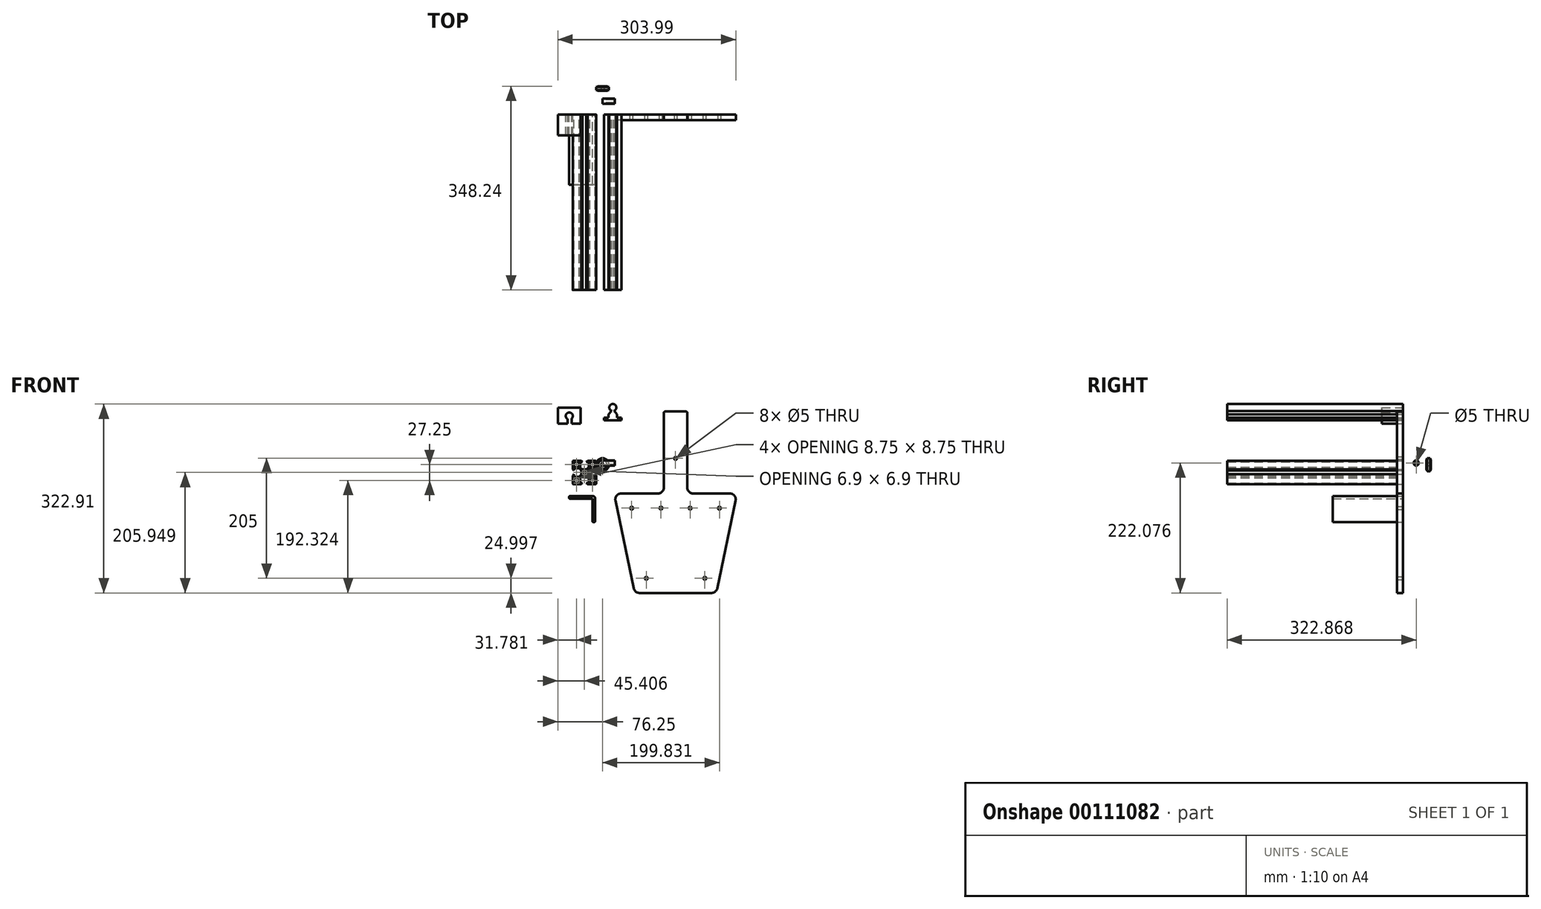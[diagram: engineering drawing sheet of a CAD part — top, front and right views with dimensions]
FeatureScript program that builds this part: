
annotation { "Feature Type Name" : "Feature", "Feature Type Description" : "" }
export const myFeature = defineFeature(function(context is Context, id is Id, definition is map)
    precondition{}
    {
        {
            var Q0;
            Q0=qCreatedBy(makeId("Front.planeOp"),FACE);
            var sketch = newSketch(context, id + "F0", { "sketchPlane" : qUnion([Q0])});
            skLineSegment(sketch, "E0", {"start": v(-49.84, 48.39) * mm, "end": v(-36.1, 48.39) * mm});
            skLineSegment(sketch, "E1", {"start": v(-36.1, 48.39) * mm, "end": v(-34.1, 46.39) * mm});
            skLineSegment(sketch, "E2", {"start": v(-34.1, 46.39) * mm, "end": v(-38.1, 46.39) * mm});
            skLineSegment(sketch, "E3", {"start": v(-48.84, 45.39) * mm, "end": v(-48.84, 38.64) * mm});
            skLineSegment(sketch, "E4", {"start": v(-48.84, 31.64) * mm, "end": v(-50.84, 33.64) * mm});
            skLineSegment(sketch, "E5", {"start": v(-50.84, 33.64) * mm, "end": v(-50.84, 47.39) * mm});
            skLineSegment(sketch, "E6", {"start": v(-50.84, 23.14) * mm, "end": v(-48.84, 25.14) * mm});
            skLineSegment(sketch, "E7", {"start": v(-48.84, 25.14) * mm, "end": v(-48.84, 22.14) * mm});
            skLineSegment(sketch, "E8", {"start": v(-47.84, 10.39) * mm, "end": v(-41.1, 10.39) * mm});
            skLineSegment(sketch, "E9", {"start": v(-34.1, 10.39) * mm, "end": v(-35.8, 8.68) * mm});
            skLineSegment(sketch, "E10", {"start": v(-36.5, 8.39) * mm, "end": v(-49.84, 8.39) * mm});
            skLineSegment(sketch, "E11", {"start": v(-50.84, 9.39) * mm, "end": v(-50.84, 23.14) * mm});
            skLineSegment(sketch, "E12", {"start": v(-25.6, 48.39) * mm, "end": v(-11.84, 48.39) * mm});
            skLineSegment(sketch, "E13", {"start": v(-10.84, 47.39) * mm, "end": v(-10.84, 33.64) * mm});
            skLineSegment(sketch, "E14", {"start": v(-10.84, 33.64) * mm, "end": v(-12.84, 31.64) * mm});
            skLineSegment(sketch, "E15", {"start": v(-12.84, 31.64) * mm, "end": v(-12.84, 34.64) * mm});
            skLineSegment(sketch, "E16", {"start": v(-13.84, 46.39) * mm, "end": v(-20.6, 46.39) * mm});
            skLineSegment(sketch, "E17", {"start": v(-27.6, 46.39) * mm, "end": v(-25.6, 48.39) * mm});
            skLineSegment(sketch, "E18", {"start": v(-10.84, 9.39) * mm, "end": v(-10.84, 22.72) * mm});
            skLineSegment(sketch, "E19", {"start": v(-11.14, 23.43) * mm, "end": v(-12.84, 25.14) * mm});
            skLineSegment(sketch, "E20", {"start": v(-12.84, 25.14) * mm, "end": v(-12.84, 22.14) * mm});
            skLineSegment(sketch, "E21", {"start": v(-13.84, 10.39) * mm, "end": v(-20.6, 10.39) * mm});
            skLineSegment(sketch, "E22", {"start": v(-27.6, 10.39) * mm, "end": v(-25.89, 8.68) * mm});
            skLineSegment(sketch, "E23", {"start": v(-25.18, 8.39) * mm, "end": v(-11.84, 8.39) * mm});
            skLineSegment(sketch, "E24", {"start": v(-48.84, 10.39) * mm, "end": v(-12.84, 46.39) * mm, "construction": true});
            skLineSegment(sketch, "E25", {"start": v(-48.84, 46.39) * mm, "end": v(-12.84, 10.39) * mm, "construction": true});
            skLineSegment(sketch, "E26", {"start": v(-40.1, 45.39) * mm, "end": v(-40.1, 38.64) * mm});
            skLineSegment(sketch, "E27", {"start": v(-41.1, 37.64) * mm, "end": v(-47.84, 37.64) * mm});
            skLineSegment(sketch, "E28", {"start": v(-13.84, 37.64) * mm, "end": v(-20.6, 37.64) * mm});
            skLineSegment(sketch, "E29", {"start": v(-21.6, 38.64) * mm, "end": v(-21.6, 45.39) * mm});
            skLineSegment(sketch, "E30", {"start": v(-47.84, 35.64) * mm, "end": v(-39.92, 35.64) * mm});
            skLineSegment(sketch, "E31", {"start": v(-38.1, 37.1) * mm, "end": v(-38.1, 46.39) * mm});
            skLineSegment(sketch, "E32", {"start": v(-23.6, 45.39) * mm, "end": v(-23.6, 37.47) * mm});
            skLineSegment(sketch, "E33", {"start": v(-21.77, 35.64) * mm, "end": v(-13.84, 35.64) * mm});
            skLineSegment(sketch, "E34.bottom", {"start": v(-34.74, 33.84) * mm, "end": v(-27.22, 33.84) * mm});
            skLineSegment(sketch, "E34.top", {"start": v(-34.46, 22.94) * mm, "end": v(-27.22, 22.94) * mm});
            skLineSegment(sketch, "E34.left", {"start": v(-36.3, 32) * mm, "end": v(-36.3, 24.77) * mm});
            skLineSegment(sketch, "E34.right", {"start": v(-25.4, 32) * mm, "end": v(-25.4, 24.77) * mm});
            skLineSegment(sketch, "E35.bottom", {"start": v(-33.3, 31.84) * mm, "end": v(-28.4, 31.84) * mm});
            skLineSegment(sketch, "E35.top", {"start": v(-33.3, 24.94) * mm, "end": v(-28.4, 24.94) * mm});
            skLineSegment(sketch, "E35.left", {"start": v(-34.3, 30.84) * mm, "end": v(-34.3, 25.94) * mm});
            skLineSegment(sketch, "E35.right", {"start": v(-27.4, 30.84) * mm, "end": v(-27.4, 25.94) * mm});
            skLineSegment(sketch, "E36", {"start": v(-23.89, 36.76) * mm, "end": v(-26.52, 34.13) * mm});
            skLineSegment(sketch, "E37", {"start": v(-25.1, 32.72) * mm, "end": v(-22.47, 35.35) * mm});
            skLineSegment(sketch, "E38", {"start": v(-35.44, 34.12) * mm, "end": v(-37.79, 36.39) * mm});
            skLineSegment(sketch, "E39", {"start": v(-47.84, 19.14) * mm, "end": v(-41.1, 19.14) * mm});
            skLineSegment(sketch, "E40", {"start": v(-40.1, 18.14) * mm, "end": v(-40.1, 11.39) * mm});
            skLineSegment(sketch, "E41", {"start": v(-47.84, 21.14) * mm, "end": v(-39.92, 21.14) * mm});
            skLineSegment(sketch, "E42", {"start": v(-38.1, 19.31) * mm, "end": v(-38.1, 11.39) * mm});
            skLineSegment(sketch, "E43", {"start": v(-21.6, 11.39) * mm, "end": v(-21.6, 18.14) * mm});
            skLineSegment(sketch, "E44", {"start": v(-20.6, 19.14) * mm, "end": v(-13.84, 19.14) * mm});
            skLineSegment(sketch, "E45", {"start": v(-21.77, 21.14) * mm, "end": v(-13.84, 21.14) * mm});
            skLineSegment(sketch, "E46", {"start": v(-23.6, 19.31) * mm, "end": v(-23.6, 11.39) * mm});
            skLineSegment(sketch, "E47", {"start": v(-35.17, 22.65) * mm, "end": v(-37.8, 20.02) * mm});
            skLineSegment(sketch, "E48", {"start": v(-39.22, 21.43) * mm, "end": v(-36.59, 24.06) * mm});
            skLineSegment(sketch, "E49", {"start": v(-22.47, 21.43) * mm, "end": v(-25.1, 24.06) * mm});
            skLineSegment(sketch, "E50", {"start": v(-36.59, 32.72) * mm, "end": v(-39.22, 35.35) * mm});
            skLineSegment(sketch, "E51", {"start": v(-23.89, 20.02) * mm, "end": v(-26.52, 22.65) * mm});
            skLineSegment(sketch, "E52.trimOffspring", {"start": v(-41.1, 46.39) * mm, "end": v(-47.84, 46.39) * mm});
            skLineSegment(sketch, "E53.trimOffspring", {"start": v(-48.84, 34.64) * mm, "end": v(-48.84, 31.64) * mm});
            skLineSegment(sketch, "E54.trimOffspring", {"start": v(-24.6, 46.39) * mm, "end": v(-27.6, 46.39) * mm});
            skLineSegment(sketch, "E55.trimOffspring", {"start": v(-12.84, 38.64) * mm, "end": v(-12.84, 45.39) * mm});
            skPoint(sketch, "E56.orphan", {"position": v(-23.6, 35.64) * mm});
            skLineSegment(sketch, "E57.trimOffspring", {"start": v(-12.84, 18.14) * mm, "end": v(-12.84, 11.39) * mm});
            skLineSegment(sketch, "E58.trimOffspring", {"start": v(-24.6, 10.39) * mm, "end": v(-27.6, 10.39) * mm});
            skLineSegment(sketch, "E59.trimOffspring", {"start": v(-37.1, 10.39) * mm, "end": v(-34.1, 10.39) * mm});
            skPoint(sketch, "E60.orphan", {"position": v(-38.1, 21.14) * mm});
            skLineSegment(sketch, "E61.trimOffspring", {"start": v(-48.84, 18.14) * mm, "end": v(-48.84, 11.39) * mm});
            skPoint(sketch, "E62.visualSharp", {"position": v(-48.84, 21.14) * mm});
            skArc(sketch, "E62.filletArc", {"start": v(-48.84, 22.14) * mm, "mid": v(-48.55, 21.43) * mm, "end": v(-47.84, 21.14) * mm});
            skPoint(sketch, "E63.visualSharp", {"position": v(-48.84, 19.14) * mm});
            skArc(sketch, "E63.filletArc", {"start": v(-47.84, 19.14) * mm, "mid": v(-48.55, 18.85) * mm, "end": v(-48.84, 18.14) * mm});
            skPoint(sketch, "E64.visualSharp", {"position": v(-40.1, 19.14) * mm});
            skArc(sketch, "E64.filletArc", {"start": v(-40.1, 18.14) * mm, "mid": v(-40.39, 18.85) * mm, "end": v(-41.1, 19.14) * mm});
            skPoint(sketch, "E65.visualSharp", {"position": v(-40.1, 10.39) * mm});
            skArc(sketch, "E65.filletArc", {"start": v(-41.1, 10.39) * mm, "mid": v(-40.39, 10.68) * mm, "end": v(-40.1, 11.39) * mm});
            skPoint(sketch, "E66.visualSharp", {"position": v(-48.84, 10.39) * mm});
            skArc(sketch, "E66.filletArc", {"start": v(-48.84, 11.39) * mm, "mid": v(-48.55, 10.68) * mm, "end": v(-47.84, 10.39) * mm});
            skPoint(sketch, "E67.visualSharp", {"position": v(-50.84, 8.39) * mm});
            skArc(sketch, "E67.filletArc", {"start": v(-50.84, 9.39) * mm, "mid": v(-50.55, 8.68) * mm, "end": v(-49.84, 8.39) * mm});
            skPoint(sketch, "E68.visualSharp", {"position": v(-36.1, 8.39) * mm});
            skArc(sketch, "E68.filletArc", {"start": v(-36.5, 8.39) * mm, "mid": v(-36.13, 8.46) * mm, "end": v(-35.8, 8.68) * mm});
            skPoint(sketch, "E69.visualSharp", {"position": v(-38.1, 10.39) * mm});
            skArc(sketch, "E69.filletArc", {"start": v(-38.1, 11.39) * mm, "mid": v(-37.8, 10.68) * mm, "end": v(-37.1, 10.39) * mm});
            skPoint(sketch, "E70.visualSharp", {"position": v(-38.1, 19.72) * mm});
            skArc(sketch, "E70.filletArc", {"start": v(-37.8, 20.02) * mm, "mid": v(-38.02, 19.7) * mm, "end": v(-38.1, 19.31) * mm});
            skPoint(sketch, "E71.visualSharp", {"position": v(-39.5, 21.14) * mm});
            skArc(sketch, "E71.filletArc", {"start": v(-39.92, 21.14) * mm, "mid": v(-39.54, 21.21) * mm, "end": v(-39.22, 21.43) * mm});
            skPoint(sketch, "E72.visualSharp", {"position": v(-34.88, 22.94) * mm});
            skArc(sketch, "E72.filletArc", {"start": v(-34.46, 22.94) * mm, "mid": v(-34.85, 22.86) * mm, "end": v(-35.17, 22.65) * mm});
            skPoint(sketch, "E73.visualSharp", {"position": v(-36.3, 24.35) * mm});
            skArc(sketch, "E73.filletArc", {"start": v(-36.59, 24.06) * mm, "mid": v(-36.37, 24.39) * mm, "end": v(-36.3, 24.77) * mm});
            skPoint(sketch, "E74.visualSharp", {"position": v(-10.84, 8.39) * mm});
            skArc(sketch, "E74.filletArc", {"start": v(-11.84, 8.39) * mm, "mid": v(-11.14, 8.68) * mm, "end": v(-10.84, 9.39) * mm});
            skPoint(sketch, "E75.visualSharp", {"position": v(-12.84, 10.39) * mm});
            skArc(sketch, "E75.filletArc", {"start": v(-13.84, 10.39) * mm, "mid": v(-13.14, 10.68) * mm, "end": v(-12.84, 11.39) * mm});
            skPoint(sketch, "E76.visualSharp", {"position": v(-21.6, 10.39) * mm});
            skArc(sketch, "E76.filletArc", {"start": v(-21.6, 11.39) * mm, "mid": v(-21.3, 10.68) * mm, "end": v(-20.6, 10.39) * mm});
            skPoint(sketch, "E77.visualSharp", {"position": v(-23.6, 10.39) * mm});
            skArc(sketch, "E77.filletArc", {"start": v(-24.6, 10.39) * mm, "mid": v(-23.89, 10.68) * mm, "end": v(-23.6, 11.39) * mm});
            skPoint(sketch, "E78.visualSharp", {"position": v(-25.6, 8.39) * mm});
            skArc(sketch, "E78.filletArc", {"start": v(-25.89, 8.68) * mm, "mid": v(-25.56, 8.46) * mm, "end": v(-25.18, 8.39) * mm});
            skPoint(sketch, "E79.visualSharp", {"position": v(-12.84, 19.14) * mm});
            skArc(sketch, "E79.filletArc", {"start": v(-12.84, 18.14) * mm, "mid": v(-13.14, 18.85) * mm, "end": v(-13.84, 19.14) * mm});
            skPoint(sketch, "E80.visualSharp", {"position": v(-21.6, 19.14) * mm});
            skArc(sketch, "E80.filletArc", {"start": v(-20.6, 19.14) * mm, "mid": v(-21.3, 18.85) * mm, "end": v(-21.6, 18.14) * mm});
            skPoint(sketch, "E81.orphan", {"position": v(-23.6, 21.14) * mm});
            skPoint(sketch, "E82.visualSharp", {"position": v(-12.84, 21.14) * mm});
            skArc(sketch, "E82.filletArc", {"start": v(-13.84, 21.14) * mm, "mid": v(-13.14, 21.43) * mm, "end": v(-12.84, 22.14) * mm});
            skPoint(sketch, "E83.visualSharp", {"position": v(-10.84, 23.14) * mm});
            skArc(sketch, "E83.filletArc", {"start": v(-10.84, 22.72) * mm, "mid": v(-10.92, 23.1) * mm, "end": v(-11.14, 23.43) * mm});
            skPoint(sketch, "E84.visualSharp", {"position": v(-23.6, 19.72) * mm});
            skArc(sketch, "E84.filletArc", {"start": v(-23.6, 19.31) * mm, "mid": v(-23.67, 19.7) * mm, "end": v(-23.89, 20.02) * mm});
            skPoint(sketch, "E85.visualSharp", {"position": v(-26.81, 22.94) * mm});
            skArc(sketch, "E85.filletArc", {"start": v(-26.52, 22.65) * mm, "mid": v(-26.84, 22.86) * mm, "end": v(-27.22, 22.94) * mm});
            skPoint(sketch, "E86.visualSharp", {"position": v(-22.18, 21.14) * mm});
            skArc(sketch, "E86.filletArc", {"start": v(-22.47, 21.43) * mm, "mid": v(-22.15, 21.21) * mm, "end": v(-21.77, 21.14) * mm});
            skPoint(sketch, "E87.visualSharp", {"position": v(-25.4, 24.35) * mm});
            skArc(sketch, "E87.filletArc", {"start": v(-25.4, 24.77) * mm, "mid": v(-25.32, 24.39) * mm, "end": v(-25.1, 24.06) * mm});
            skPoint(sketch, "E88.visualSharp", {"position": v(-27.4, 24.94) * mm});
            skArc(sketch, "E88.filletArc", {"start": v(-28.4, 24.94) * mm, "mid": v(-27.69, 25.23) * mm, "end": v(-27.4, 25.94) * mm});
            skPoint(sketch, "E89.visualSharp", {"position": v(-34.3, 24.94) * mm});
            skArc(sketch, "E89.filletArc", {"start": v(-34.3, 25.94) * mm, "mid": v(-34, 25.23) * mm, "end": v(-33.3, 24.94) * mm});
            skPoint(sketch, "E90.visualSharp", {"position": v(-34.3, 31.84) * mm});
            skArc(sketch, "E90.filletArc", {"start": v(-33.3, 31.84) * mm, "mid": v(-34, 31.54) * mm, "end": v(-34.3, 30.84) * mm});
            skPoint(sketch, "E91.visualSharp", {"position": v(-27.4, 31.84) * mm});
            skArc(sketch, "E91.filletArc", {"start": v(-27.4, 30.84) * mm, "mid": v(-27.69, 31.54) * mm, "end": v(-28.4, 31.84) * mm});
            skPoint(sketch, "E92.visualSharp", {"position": v(-25.4, 32.42) * mm});
            skArc(sketch, "E92.filletArc", {"start": v(-25.1, 32.72) * mm, "mid": v(-25.32, 32.4) * mm, "end": v(-25.4, 32) * mm});
            skPoint(sketch, "E93.visualSharp", {"position": v(-22.18, 35.64) * mm});
            skArc(sketch, "E93.filletArc", {"start": v(-21.77, 35.64) * mm, "mid": v(-22.15, 35.56) * mm, "end": v(-22.47, 35.35) * mm});
            skPoint(sketch, "E94.visualSharp", {"position": v(-12.84, 35.64) * mm});
            skArc(sketch, "E94.filletArc", {"start": v(-12.84, 34.64) * mm, "mid": v(-13.14, 35.35) * mm, "end": v(-13.84, 35.64) * mm});
            skPoint(sketch, "E95.visualSharp", {"position": v(-12.84, 37.64) * mm});
            skArc(sketch, "E95.filletArc", {"start": v(-13.84, 37.64) * mm, "mid": v(-13.14, 37.93) * mm, "end": v(-12.84, 38.64) * mm});
            skPoint(sketch, "E96.visualSharp", {"position": v(-21.6, 37.64) * mm});
            skArc(sketch, "E96.filletArc", {"start": v(-21.6, 38.64) * mm, "mid": v(-21.3, 37.93) * mm, "end": v(-20.6, 37.64) * mm});
            skPoint(sketch, "E97.visualSharp", {"position": v(-23.6, 37.05) * mm});
            skArc(sketch, "E97.filletArc", {"start": v(-23.89, 36.76) * mm, "mid": v(-23.67, 37.08) * mm, "end": v(-23.6, 37.47) * mm});
            skPoint(sketch, "E98.visualSharp", {"position": v(-26.81, 33.84) * mm});
            skArc(sketch, "E98.filletArc", {"start": v(-27.22, 33.84) * mm, "mid": v(-26.84, 33.91) * mm, "end": v(-26.52, 34.13) * mm});
            skPoint(sketch, "E99.visualSharp", {"position": v(-35.15, 33.84) * mm});
            skArc(sketch, "E99.filletArc", {"start": v(-35.44, 34.12) * mm, "mid": v(-35.12, 33.91) * mm, "end": v(-34.74, 33.84) * mm});
            skPoint(sketch, "E100.visualSharp", {"position": v(-38.1, 36.68) * mm});
            skArc(sketch, "E100.filletArc", {"start": v(-38.1, 37.1) * mm, "mid": v(-38.01, 36.72) * mm, "end": v(-37.79, 36.39) * mm});
            skPoint(sketch, "E101.visualSharp", {"position": v(-36.3, 32.42) * mm});
            skArc(sketch, "E101.filletArc", {"start": v(-36.3, 32) * mm, "mid": v(-36.37, 32.4) * mm, "end": v(-36.59, 32.72) * mm});
            skPoint(sketch, "E102.visualSharp", {"position": v(-39.5, 35.64) * mm});
            skArc(sketch, "E102.filletArc", {"start": v(-39.22, 35.35) * mm, "mid": v(-39.54, 35.56) * mm, "end": v(-39.92, 35.64) * mm});
            skPoint(sketch, "E103.visualSharp", {"position": v(-12.84, 46.39) * mm});
            skArc(sketch, "E103.filletArc", {"start": v(-12.84, 45.39) * mm, "mid": v(-13.14, 46.1) * mm, "end": v(-13.84, 46.39) * mm});
            skPoint(sketch, "E104.visualSharp", {"position": v(-10.84, 48.39) * mm});
            skArc(sketch, "E104.filletArc", {"start": v(-10.84, 47.39) * mm, "mid": v(-11.14, 48.1) * mm, "end": v(-11.84, 48.39) * mm});
            skPoint(sketch, "E105.visualSharp", {"position": v(-23.6, 46.39) * mm});
            skArc(sketch, "E105.filletArc", {"start": v(-23.6, 45.39) * mm, "mid": v(-23.89, 46.1) * mm, "end": v(-24.6, 46.39) * mm});
            skPoint(sketch, "E106.visualSharp", {"position": v(-21.6, 46.39) * mm});
            skArc(sketch, "E106.filletArc", {"start": v(-20.6, 46.39) * mm, "mid": v(-21.3, 46.1) * mm, "end": v(-21.6, 45.39) * mm});
            skPoint(sketch, "E107.visualSharp", {"position": v(-48.84, 35.64) * mm});
            skArc(sketch, "E107.filletArc", {"start": v(-47.84, 35.64) * mm, "mid": v(-48.55, 35.35) * mm, "end": v(-48.84, 34.64) * mm});
            skPoint(sketch, "E108.visualSharp", {"position": v(-48.84, 37.64) * mm});
            skArc(sketch, "E108.filletArc", {"start": v(-48.84, 38.64) * mm, "mid": v(-48.55, 37.93) * mm, "end": v(-47.84, 37.64) * mm});
            skPoint(sketch, "E109.visualSharp", {"position": v(-50.84, 48.39) * mm});
            skArc(sketch, "E109.filletArc", {"start": v(-49.84, 48.39) * mm, "mid": v(-50.55, 48.1) * mm, "end": v(-50.84, 47.39) * mm});
            skPoint(sketch, "E110.visualSharp", {"position": v(-48.84, 46.39) * mm});
            skArc(sketch, "E110.filletArc", {"start": v(-47.84, 46.39) * mm, "mid": v(-48.55, 46.1) * mm, "end": v(-48.84, 45.39) * mm});
            skPoint(sketch, "E111.visualSharp", {"position": v(-40.1, 46.39) * mm});
            skArc(sketch, "E111.filletArc", {"start": v(-40.1, 45.39) * mm, "mid": v(-40.39, 46.1) * mm, "end": v(-41.1, 46.39) * mm});
            skPoint(sketch, "E112.visualSharp", {"position": v(-40.1, 37.64) * mm});
            skArc(sketch, "E112.filletArc", {"start": v(-41.1, 37.64) * mm, "mid": v(-40.39, 37.93) * mm, "end": v(-40.1, 38.64) * mm});
            skSolve(sketch);
        }
        {
            var Q0;
            Q0=makeQuery(id+"F0.imprint","IMPRINT",FACE,{"disambiguationData":[TD([[makeQuery(id+"F0.imprint","IMPRINT",EDGE,{"derivedFrom":sQuery(id+"F0.wireOp",EDGE,"E0")}),-1.0]])]});
            extrude(context, id + "F1", {"entities" : qUnion([Q0]), "depth" : 300 * mm});
        }
        {
            var Q0;
            Q0=qCreatedBy(makeId("Front.planeOp"),FACE);
            var sketch = newSketch(context, id + "F2", { "sketchPlane" : qUnion([Q0])});
            skLineSegment(sketch, "E113", {"start": v(-55.84, -12.26) * mm, "end": v(-15.84, -12.26) * mm});
            skLineSegment(sketch, "E114", {"start": v(-12.84, -15.26) * mm, "end": v(-12.84, -55.26) * mm});
            skLineSegment(sketch, "E115", {"start": v(-13.84, -56.26) * mm, "end": v(-15.84, -56.26) * mm});
            skLineSegment(sketch, "E116", {"start": v(-16.84, -55.26) * mm, "end": v(-16.84, -17.26) * mm});
            skLineSegment(sketch, "E117", {"start": v(-17.84, -16.26) * mm, "end": v(-55.84, -16.26) * mm});
            skLineSegment(sketch, "E118", {"start": v(-56.84, -15.26) * mm, "end": v(-56.84, -13.26) * mm});
            skPoint(sketch, "E119.visualSharp", {"position": v(-56.84, -12.26) * mm});
            skArc(sketch, "E119.filletArc", {"start": v(-55.84, -12.26) * mm, "mid": v(-56.55, -12.56) * mm, "end": v(-56.84, -13.26) * mm});
            skPoint(sketch, "E120.visualSharp", {"position": v(-56.84, -16.26) * mm});
            skArc(sketch, "E120.filletArc", {"start": v(-56.84, -15.26) * mm, "mid": v(-56.55, -15.97) * mm, "end": v(-55.84, -16.26) * mm});
            skPoint(sketch, "E121.visualSharp", {"position": v(-16.84, -16.26) * mm});
            skArc(sketch, "E121.filletArc", {"start": v(-16.84, -17.26) * mm, "mid": v(-17.13, -16.56) * mm, "end": v(-17.84, -16.26) * mm});
            skPoint(sketch, "E122.visualSharp", {"position": v(-12.84, -56.26) * mm});
            skArc(sketch, "E122.filletArc", {"start": v(-13.84, -56.26) * mm, "mid": v(-13.13, -55.97) * mm, "end": v(-12.84, -55.26) * mm});
            skPoint(sketch, "E123.visualSharp", {"position": v(-16.84, -56.26) * mm});
            skArc(sketch, "E123.filletArc", {"start": v(-16.84, -55.26) * mm, "mid": v(-16.55, -55.97) * mm, "end": v(-15.84, -56.26) * mm});
            skPoint(sketch, "E124.visualSharp", {"position": v(-12.84, -12.26) * mm});
            skArc(sketch, "E124.filletArc", {"start": v(-12.84, -15.26) * mm, "mid": v(-13.72, -13.14) * mm, "end": v(-15.84, -12.26) * mm});
            skSolve(sketch);
        }
        {
            var Q0;
            Q0=makeQuery(id+"F2.imprint","IMPRINT",FACE,{"disambiguationData":[TD([[makeQuery(id+"F2.imprint","IMPRINT",EDGE,{"derivedFrom":sQuery(id+"F2.wireOp",EDGE,"E113")}),-1.0]])]});
            extrude(context, id + "F3", {"entities" : qUnion([Q0]), "depth" : 120 * mm});
        }
        {
            var Q0;
            Q0=qCreatedBy(makeId("Front.planeOp"),FACE);
            var sketch = newSketch(context, id + "F4", { "sketchPlane" : qUnion([Q0])});
            skLineSegment(sketch, "E125", {"start": v(-8.08, -7.56) * mm, "end": v(54.83, -7.56) * mm});
            skLineSegment(sketch, "E126", {"start": v(187.53, -19.6) * mm, "end": v(156.28, -169.6) * mm});
            skLineSegment(sketch, "E127", {"start": v(146.5, -177.56) * mm, "end": v(23.17, -177.56) * mm});
            skLineSegment(sketch, "E128", {"start": v(13.38, -169.6) * mm, "end": v(-17.87, -19.6) * mm});
            skPoint(sketch, "E129", {"position": v(84.83, -7.56) * mm});
            skPoint(sketch, "E130", {"position": v(84.83, -177.56) * mm});
            skLineSegment(sketch, "E131", {"start": v(84.83, -177.56) * mm, "end": v(84.83, -7.56) * mm, "construction": true});
            skPoint(sketch, "E132.visualSharp", {"position": v(190.04, -7.56) * mm});
            skArc(sketch, "E132.filletArc", {"start": v(187.53, -19.6) * mm, "mid": v(185.5, -11.25) * mm, "end": v(177.74, -7.56) * mm});
            skPoint(sketch, "E133.visualSharp", {"position": v(-20.38, -7.56) * mm});
            skArc(sketch, "E133.filletArc", {"start": v(-8.08, -7.56) * mm, "mid": v(-15.84, -11.25) * mm, "end": v(-17.87, -19.6) * mm});
            skPoint(sketch, "E134.visualSharp", {"position": v(15.04, -177.56) * mm});
            skArc(sketch, "E134.filletArc", {"start": v(13.38, -169.6) * mm, "mid": v(16.86, -175.32) * mm, "end": v(23.17, -177.56) * mm});
            skPoint(sketch, "E135.visualSharp", {"position": v(154.62, -177.56) * mm});
            skArc(sketch, "E135.filletArc", {"start": v(146.5, -177.56) * mm, "mid": v(152.8, -175.32) * mm, "end": v(156.28, -169.6) * mm});
            skLineSegment(sketch, "E136", {"start": v(9.83, -152.56) * mm, "end": v(159.83, -152.56) * mm, "construction": true});
            skLineSegment(sketch, "E137", {"start": v(-15.17, -32.56) * mm, "end": v(184.83, -32.56) * mm, "construction": true});
            skCircle(sketch, "E138", {"center": v(9.83, -32.56) * mm, "radius": 2.5 * mm});
            skCircle(sketch, "E139", {"center": v(59.83, -32.56) * mm, "radius": 2.5 * mm});
            skCircle(sketch, "E140", {"center": v(109.83, -32.56) * mm, "radius": 2.5 * mm});
            skCircle(sketch, "E141", {"center": v(159.83, -32.56) * mm, "radius": 2.5 * mm});
            skCircle(sketch, "E142", {"center": v(34.83, -152.56) * mm, "radius": 2.5 * mm});
            skCircle(sketch, "E143", {"center": v(134.83, -152.56) * mm, "radius": 2.5 * mm});
            skLineSegment(sketch, "E144", {"start": v(34.83, -141.56) * mm, "end": v(134.83, -141.56) * mm, "construction": true});
            skLineSegment(sketch, "E145", {"start": v(9.83, -59.91) * mm, "end": v(59.83, -59.91) * mm, "construction": true});
            skLineSegment(sketch, "E146", {"start": v(59.83, -59.91) * mm, "end": v(109.83, -59.91) * mm, "construction": true});
            skLineSegment(sketch, "E147", {"start": v(109.83, -59.91) * mm, "end": v(159.83, -59.91) * mm, "construction": true});
            skPoint(sketch, "E148", {"position": v(84.83, -59.91) * mm});
            skPoint(sketch, "E149", {"position": v(84.83, -141.56) * mm});
            skPoint(sketch, "E150", {"position": v(34.83, -59.91) * mm});
            skPoint(sketch, "E151", {"position": v(134.83, -59.91) * mm});
            skLineSegment(sketch, "E152", {"start": v(64.83, 2.44) * mm, "end": v(64.83, 130.44) * mm});
            skLineSegment(sketch, "E153", {"start": v(66.83, 132.44) * mm, "end": v(102.83, 132.44) * mm});
            skLineSegment(sketch, "E154", {"start": v(104.83, 130.44) * mm, "end": v(104.83, 2.44) * mm});
            skLineSegment(sketch, "E155.trimOffspring", {"start": v(114.83, -7.56) * mm, "end": v(177.74, -7.56) * mm});
            skPoint(sketch, "E156", {"position": v(84.83, 132.44) * mm});
            skPoint(sketch, "E157.visualSharp", {"position": v(104.83, -7.56) * mm});
            skArc(sketch, "E157.filletArc", {"start": v(104.83, 2.44) * mm, "mid": v(107.76, -4.63) * mm, "end": v(114.83, -7.56) * mm});
            skPoint(sketch, "E158.visualSharp", {"position": v(64.83, -7.56) * mm});
            skArc(sketch, "E158.filletArc", {"start": v(54.83, -7.56) * mm, "mid": v(61.9, -4.63) * mm, "end": v(64.83, 2.44) * mm});
            skPoint(sketch, "E159.visualSharp", {"position": v(104.83, 132.44) * mm});
            skArc(sketch, "E159.filletArc", {"start": v(104.83, 130.44) * mm, "mid": v(104.25, 131.85) * mm, "end": v(102.83, 132.44) * mm});
            skPoint(sketch, "E160.visualSharp", {"position": v(64.83, 132.44) * mm});
            skArc(sketch, "E160.filletArc", {"start": v(66.83, 132.44) * mm, "mid": v(65.42, 131.85) * mm, "end": v(64.83, 130.44) * mm});
            skSolve(sketch);
        }
        {
            var Q0;
            Q0=makeQuery(id+"F4.imprint","IMPRINT",FACE,{"disambiguationData":[TD([[makeQuery(id+"F4.imprint","IMPRINT",EDGE,{"derivedFrom":sQuery(id+"F4.wireOp",EDGE,"E125")}),-1.0]])]});
            extrude(context, id + "F5", {"entities" : qUnion([Q0]), "depth" : 10 * mm});
        }
        {
            var Q0;
            Q0=makeQuery(id+"F5.opExtrude","SWEPT_BODY",BODY,{"disambiguationData":[OSD([sQuery(id+"F4.wireOp",EDGE,"E125"),sQuery(id+"F4.wireOp",EDGE,"E126"),sQuery(id+"F4.wireOp",EDGE,"E127"),sQuery(id+"F4.wireOp",EDGE,"E128"),sQuery(id+"F4.wireOp",EDGE,"E132.filletArc"),sQuery(id+"F4.wireOp",EDGE,"E133.filletArc"),sQuery(id+"F4.wireOp",EDGE,"E134.filletArc"),sQuery(id+"F4.wireOp",EDGE,"E135.filletArc"),sQuery(id+"F4.wireOp",EDGE,"E138"),sQuery(id+"F4.wireOp",EDGE,"E139"),sQuery(id+"F4.wireOp",EDGE,"E140"),sQuery(id+"F4.wireOp",EDGE,"E141"),sQuery(id+"F4.wireOp",EDGE,"E142"),sQuery(id+"F4.wireOp",EDGE,"E143"),sQuery(id+"F4.wireOp",EDGE,"E152"),sQuery(id+"F4.wireOp",EDGE,"E153"),sQuery(id+"F4.wireOp",EDGE,"E154"),sQuery(id+"F4.wireOp",EDGE,"E155.trimOffspring"),sQuery(id+"F4.wireOp",EDGE,"E157.filletArc"),sQuery(id+"F4.wireOp",EDGE,"E158.filletArc"),sQuery(id+"F4.wireOp",EDGE,"E159.filletArc"),sQuery(id+"F4.wireOp",EDGE,"E160.filletArc")])]});
            transform(context, id + "F6", {"entities" : qUnion([Q0]), "transformType" : TransformType.TRANSLATION_3D, "dx" : 40 * mm, "dy" : 0 * mm, "dz" : 0 * mm, "makeCopy" : false});
        }
        {
            var Q0;
            Q0=qCreatedBy(makeId("Right.planeOp"),FACE);
            var sketch = newSketch(context, id + "F7", { "sketchPlane" : qUnion([Q0])});
            skLineSegment(sketch, "E161", {"start": v(41.74, 52.7) * mm, "end": v(46.74, 52.7) * mm});
            skLineSegment(sketch, "E162", {"start": v(46.74, 52.7) * mm, "end": v(48.24, 49.13) * mm});
            skLineSegment(sketch, "E163", {"start": v(48.24, 49.13) * mm, "end": v(48.24, 44.2) * mm});
            skLineSegment(sketch, "E164", {"start": v(41.74, 52.7) * mm, "end": v(40.24, 49.13) * mm});
            skLineSegment(sketch, "E165", {"start": v(40.24, 49.13) * mm, "end": v(40.24, 44.2) * mm});
            skLineSegment(sketch, "E166", {"start": v(40.24, 44.2) * mm, "end": v(48.24, 44.2) * mm});
            skPoint(sketch, "E167", {"position": v(44.24, 44.2) * mm});
            skPoint(sketch, "E168", {"position": v(44.24, 52.7) * mm});
            skLineSegment(sketch, "E169", {"start": v(40.24, 41.7) * mm, "end": v(48.24, 41.7) * mm, "construction": true});
            skSolve(sketch);
        }
        {
            var Q0;
            Q0=makeQuery(id+"F7.imprint","IMPRINT",FACE,{"disambiguationData":[TD([[makeQuery(id+"F7.imprint","IMPRINT",EDGE,{"derivedFrom":sQuery(id+"F7.wireOp",EDGE,"E161")}),-1.0]])]});
            var Q1;
            Q1=sQuery(id+"F7.wireOp",EDGE,"E169");
            revolve(context, id + "F8", {"entities" : qUnion([Q0]), "axis" : qUnion([Q1]), "revolveType" : RevolveType.FULL});
        }
        {
            var Q0;
            Q0=qCreatedBy(makeId("Right.planeOp"),FACE);
            var sketch = newSketch(context, id + "F9", { "sketchPlane" : qUnion([Q0])});
            skLineSegment(sketch, "E170.0", {"start": v(40.24, 34.26) * mm, "end": v(40.24, 49.13) * mm, "construction": true});
            skPoint(sketch, "E171", {"position": v(40.24, 60.88) * mm});
            skLineSegment(sketch, "E172", {"start": v(40.24, 60.88) * mm, "end": v(19.24, 60.88) * mm, "construction": true});
            skLineSegment(sketch, "E173", {"start": v(44.24, 65.5) * mm, "end": v(19.24, 65.5) * mm, "construction": true});
            skPoint(sketch, "E174", {"position": v(46.74, 52.7) * mm});
            skLineSegment(sketch, "E175", {"start": v(41.74, 52.7) * mm, "end": v(46.74, 52.7) * mm, "construction": true});
            skPoint(sketch, "E176", {"position": v(44.24, 52.7) * mm});
            skCircle(sketch, "E177", {"center": v(22.87, 44.52) * mm, "radius": 2.5 * mm});
            skCircle(sketch, "E178", {"center": v(22.87, 44.52) * mm, "radius": 4.5 * mm});
            skSolve(sketch);
        }
        {
            var Q0;
            Q0=makeQuery(id+"F9.imprint","IMPRINT",FACE,{"disambiguationData":[TD([[makeQuery(id+"F9.imprint","IMPRINT",EDGE,{"derivedFrom":sQuery(id+"F9.wireOp",EDGE,"E177")}),-1.0]])]});
            extrude(context, id + "F10", {"entities" : qUnion([Q0]), "depth" : 21 * mm});
        }
        {
            var Q0;
            Q0=makeQuery(id+"F5.opExtrude","CAP_FACE",FACE,{"disambiguationData":[OSD([sQuery(id+"F4.wireOp",EDGE,"E125"),sQuery(id+"F4.wireOp",EDGE,"E126"),sQuery(id+"F4.wireOp",EDGE,"E127"),sQuery(id+"F4.wireOp",EDGE,"E128"),sQuery(id+"F4.wireOp",EDGE,"E132.filletArc"),sQuery(id+"F4.wireOp",EDGE,"E133.filletArc"),sQuery(id+"F4.wireOp",EDGE,"E134.filletArc"),sQuery(id+"F4.wireOp",EDGE,"E135.filletArc"),sQuery(id+"F4.wireOp",EDGE,"E138"),sQuery(id+"F4.wireOp",EDGE,"E139"),sQuery(id+"F4.wireOp",EDGE,"E140"),sQuery(id+"F4.wireOp",EDGE,"E141"),sQuery(id+"F4.wireOp",EDGE,"E142"),sQuery(id+"F4.wireOp",EDGE,"E143"),sQuery(id+"F4.wireOp",EDGE,"E152"),sQuery(id+"F4.wireOp",EDGE,"E153"),sQuery(id+"F4.wireOp",EDGE,"E154"),sQuery(id+"F4.wireOp",EDGE,"E155.trimOffspring"),sQuery(id+"F4.wireOp",EDGE,"E157.filletArc"),sQuery(id+"F4.wireOp",EDGE,"E158.filletArc"),sQuery(id+"F4.wireOp",EDGE,"E159.filletArc"),sQuery(id+"F4.wireOp",EDGE,"E160.filletArc")])],"isStart":false});
            var sketch = newSketch(context, id + "F11", { "sketchPlane" : qUnion([Q0])});
            skPoint(sketch, "E179", {"position": v(124.83, 132.44) * mm});
            skLineSegment(sketch, "E180", {"start": v(124.83, 132.44) * mm, "end": v(124.83, 52.44) * mm, "construction": true});
            skCircle(sketch, "E181", {"center": v(124.83, 52.44) * mm, "radius": 2.5 * mm});
            skSolve(sketch);
        }
        {
            var Q0;
            Q0=makeQuery(id+"F11.imprint","IMPRINT",FACE,{"disambiguationData":[TD([[makeQuery(id+"F11.imprint","IMPRINT",EDGE,{"derivedFrom":sQuery(id+"F11.wireOp",EDGE,"E181")}),1.0]])]});
            extrude(context, id + "F12", {"entities" : qUnion([Q0]), "operationType" : NewBodyOperationType.REMOVE, "endBound" : BoundingType.UP_TO_NEXT, "oppositeDirection" : true, "depth" : 25 * mm});
        }
        {
            var Q0;
            Q0=qCreatedBy(makeId("Front.planeOp"),FACE);
            var sketch = newSketch(context, id + "F13", { "sketchPlane" : qUnion([Q0])});
            skCircle(sketch, "E182", {"center": v(17.64, 139.35) * mm, "radius": 6 * mm});
            skLineSegment(sketch, "E183.bottom", {"start": v(2.64, 122) * mm, "end": v(32.64, 122) * mm});
            skLineSegment(sketch, "E183.top", {"start": v(2.64, 117.35) * mm, "end": v(32.64, 117.35) * mm});
            skLineSegment(sketch, "E183.left", {"start": v(2.64, 122) * mm, "end": v(2.64, 117.35) * mm});
            skLineSegment(sketch, "E183.right", {"start": v(32.64, 122) * mm, "end": v(32.64, 117.35) * mm});
            skLineSegment(sketch, "E184.bottom", {"start": v(25.14, 127.53) * mm, "end": v(10.14, 127.53) * mm});
            skLineSegment(sketch, "E184.top", {"start": v(25.14, 122) * mm, "end": v(10.14, 122) * mm});
            skLineSegment(sketch, "E184.left", {"start": v(25.14, 127.53) * mm, "end": v(25.14, 122) * mm});
            skLineSegment(sketch, "E184.right", {"start": v(10.14, 127.53) * mm, "end": v(10.14, 122) * mm});
            skLineSegment(sketch, "E185", {"start": v(10.14, 127.53) * mm, "end": v(15.14, 133.5) * mm});
            skLineSegment(sketch, "E186", {"start": v(15.14, 133.5) * mm, "end": v(20.13, 133.52) * mm});
            skLineSegment(sketch, "E187", {"start": v(20.13, 133.52) * mm, "end": v(25.14, 127.53) * mm});
            skPoint(sketch, "E188", {"position": v(17.64, 127.53) * mm});
            skPoint(sketch, "E189", {"position": v(17.64, 133.52) * mm});
            skPoint(sketch, "E190", {"position": v(17.64, 122) * mm});
            skPoint(sketch, "E191", {"position": v(17.64, 145.35) * mm});
            skSolve(sketch);
        }
        {
            var Q0;
            Q0=qCreatedBy(makeId("Front.planeOp"),FACE);
            var sketch = newSketch(context, id + "F14", { "sketchPlane" : qUnion([Q0])});
            skArc(sketch, "E192", {"start": v(-52.9, 120.27) * mm, "mid": v(-57.2, 130.84) * mm, "end": v(-59.9, 119.74) * mm});
            skLineSegment(sketch, "E193", {"start": v(-59.9, 119.74) * mm, "end": v(-59.9, 112.05) * mm});
            skLineSegment(sketch, "E194", {"start": v(-59.9, 112.05) * mm, "end": v(-76.25, 112.05) * mm});
            skLineSegment(sketch, "E195", {"start": v(-76.25, 112.05) * mm, "end": v(-76.25, 139.05) * mm});
            skLineSegment(sketch, "E196", {"start": v(-76.25, 139.05) * mm, "end": v(-37.25, 139.05) * mm});
            skLineSegment(sketch, "E197", {"start": v(-37.25, 139.05) * mm, "end": v(-37.25, 112.05) * mm});
            skLineSegment(sketch, "E198", {"start": v(-37.25, 112.05) * mm, "end": v(-52.9, 112.05) * mm});
            skLineSegment(sketch, "E199", {"start": v(-52.9, 112.05) * mm, "end": v(-52.9, 120.27) * mm});
            skPoint(sketch, "E200", {"position": v(-56.75, 139.05) * mm});
            skPoint(sketch, "E201", {"position": v(-56.75, 130.84) * mm});
            skPoint(sketch, "E201.positionSnap0", {"position": v(-57.2, 130.84) * mm});
            skLineSegment(sketch, "E202", {"start": v(-57.2, 130.84) * mm, "end": v(-56.75, 139.05) * mm, "construction": true});
            skSolve(sketch);
        }
        {
            var Q0;
            Q0=makeQuery(id+"F14.imprint","IMPRINT",FACE,{"disambiguationData":[TD([[makeQuery(id+"F14.imprint","IMPRINT",EDGE,{"derivedFrom":sQuery(id+"F14.wireOp",EDGE,"E192")}),-1.0]])]});
            extrude(context, id + "F15", {"entities" : qUnion([Q0]), "depth" : 36 * mm});
        }
        {
            var Q0;
            Q0=qSketchRegion(id+"F13",true);
            extrude(context, id + "F16", {"entities" : qUnion([Q0]), "depth" : 300 * mm});
        }
    });
